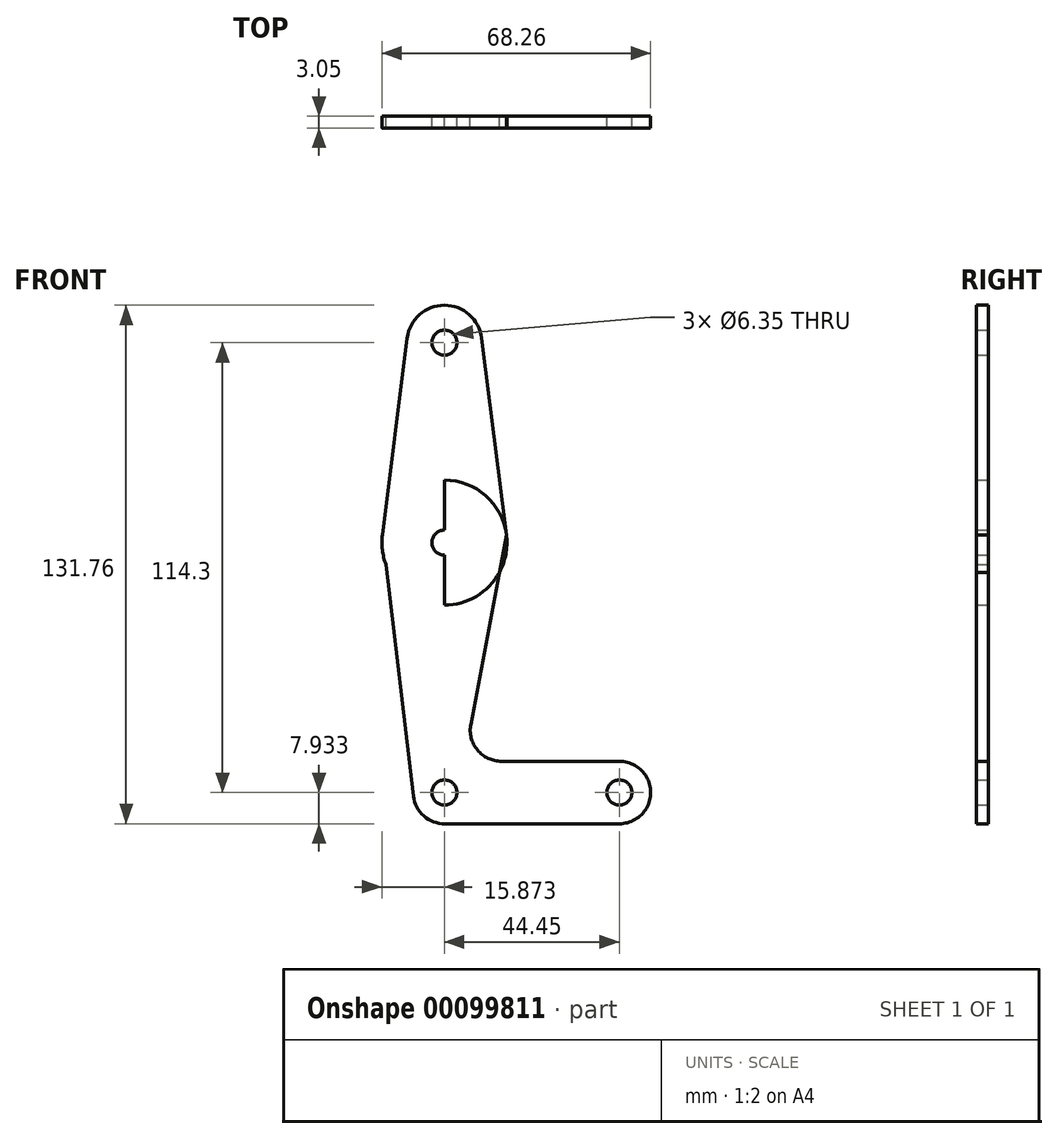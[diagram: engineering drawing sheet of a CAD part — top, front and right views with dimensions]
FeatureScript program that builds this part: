
annotation { "Feature Type Name" : "Feature", "Feature Type Description" : "" }
export const myFeature = defineFeature(function(context is Context, id is Id, definition is map)
    precondition{}
    {
        {
            var Q0;
            Q0=qCreatedBy(makeId("Front.planeOp"),FACE);
            var sketch = newSketch(context, id + "F0", { "sketchPlane" : qUnion([Q0])});
            skLineSegment(sketch, "E0", {"start": v(7.52, 95.91) * mm, "end": v(7.52, -18.39) * mm});
            skLineSegment(sketch, "E1", {"start": v(7.52, -18.39) * mm, "end": v(51.97, -18.39) * mm});
            skCircle(sketch, "E2", {"center": v(7.52, 95.91) * mm, "radius": 9.53 * mm});
            skCircle(sketch, "E3", {"center": v(7.52, 45.11) * mm, "radius": 15.88 * mm});
            skCircle(sketch, "E4", {"center": v(7.52, -18.39) * mm, "radius": 7.94 * mm});
            skCircle(sketch, "E5", {"center": v(51.97, -18.39) * mm, "radius": 7.94 * mm});
            skLineSegment(sketch, "E6", {"start": v(-1.93, 97.1) * mm, "end": v(-8.23, 47.1) * mm});
            skLineSegment(sketch, "E7", {"start": v(-8.23, 47.1) * mm, "end": v(-0.36, -19.32) * mm});
            skLineSegment(sketch, "E8", {"start": v(14.22, -1.03) * mm, "end": v(23.27, 47.1) * mm});
            skLineSegment(sketch, "E9", {"start": v(23.27, 47.1) * mm, "end": v(16.97, 97.1) * mm});
            skLineSegment(sketch, "E10", {"start": v(22.03, -10.45) * mm, "end": v(51.97, -10.45) * mm});
            skLineSegment(sketch, "E11", {"start": v(7.6, -26.32) * mm, "end": v(51.97, -26.32) * mm});
            skCircle(sketch, "E12", {"center": v(7.52, 95.91) * mm, "radius": 3.18 * mm});
            skCircle(sketch, "E13", {"center": v(7.52, 45.11) * mm, "radius": 3.18 * mm});
            skCircle(sketch, "E14", {"center": v(7.52, -18.39) * mm, "radius": 3.18 * mm});
            skCircle(sketch, "E15", {"center": v(51.97, -18.39) * mm, "radius": 3.18 * mm});
            skArc(sketch, "E16.filletArc", {"start": v(14.22, -1.03) * mm, "mid": v(15.91, -7.57) * mm, "end": v(22.03, -10.45) * mm});
            skSolve(sketch);
        }
        {
            var Q0;
            {var subQ3=sQuery(id+"F0.wireOp",EDGE,"E4");var subQ7=sQuery(id+"F0.wireOp",EDGE,"E0");var subQ8=makeQuery(id+"F0.imprint","INTERSECT",VERTEX,{"derivedFrom":[subQ7,subQ3]});Q0=makeQuery(id+"F0.imprint","IMPRINT",FACE,{"disambiguationData":[TD([[makeQuery(id+"F0.imprint","IMPRINT",EDGE,{"disambiguationData":[TD([[subQ8,-1.0]])],"derivedFrom":subQ7}),-1.0]])]});}
            var Q1;
            {var subQ10=sQuery(id+"F0.wireOp",EDGE,"E10");Q1=makeQuery(id+"F0.imprint","IMPRINT",FACE,{"disambiguationData":[TD([[makeQuery(id+"F0.imprint","IMPRINT",EDGE,{"derivedFrom":subQ10}),-1.0]])]});}
            var Q2;
            Q2=makeQuery(id+"F0.imprint","IMPRINT",FACE,{"disambiguationData":[TD([[makeQuery(id+"F0.imprint","IMPRINT",EDGE,{"derivedFrom":sQuery(id+"F0.wireOp",EDGE,"E12")}),-1.0]])]});
            var Q3;
            Q3=makeQuery(id+"F0.imprint","IMPRINT",FACE,{"disambiguationData":[TD([[makeQuery(id+"F0.imprint","IMPRINT",EDGE,{"derivedFrom":sQuery(id+"F0.wireOp",EDGE,"E15")}),-1.0]])]});
            var Q4;
            {var subQ1=sQuery(id+"F0.wireOp",EDGE,"E3");var subQ3=sQuery(id+"F0.wireOp",EDGE,"E0");var subQ4=makeQuery(id+"F0.imprint","INTERSECT",VERTEX,{"disambiguationData":[OD(0.0)],"derivedFrom":[subQ3,subQ1]});Q4=makeQuery(id+"F0.imprint","IMPRINT",FACE,{"disambiguationData":[TD([[makeQuery(id+"F0.imprint","IMPRINT",EDGE,{"disambiguationData":[TD([[subQ4,-1.0]])],"derivedFrom":subQ3}),1.0]])]});}
            var Q5;
            {var subQ0=sQuery(id+"F0.wireOp",EDGE,"E8");var subQ1=sQuery(id+"F0.wireOp",EDGE,"E3");var subQ3=makeQuery(id+"F0.imprint","INTERSECT",VERTEX,{"derivedFrom":[subQ1,subQ0]});Q5=makeQuery(id+"F0.imprint","IMPRINT",FACE,{"disambiguationData":[TD([[makeQuery(id+"F0.imprint","IMPRINT",EDGE,{"disambiguationData":[TD([[subQ3,-1.0]])],"derivedFrom":subQ1}),1.0]])]});}
            var Q6;
            {var subQ5=sQuery(id+"F0.wireOp",EDGE,"E9");Q6=makeQuery(id+"F0.imprint","IMPRINT",FACE,{"disambiguationData":[TD([[makeQuery(id+"F0.imprint","IMPRINT",EDGE,{"derivedFrom":subQ5}),1.0]])]});}
            var Q7;
            {var subQ0=sQuery(id+"F0.wireOp",EDGE,"E4");var subQ1=sQuery(id+"F0.wireOp",EDGE,"E0");var subQ2=makeQuery(id+"F0.imprint","INTERSECT",VERTEX,{"derivedFrom":[subQ1,subQ0]});Q7=makeQuery(id+"F0.imprint","IMPRINT",FACE,{"disambiguationData":[TD([[makeQuery(id+"F0.imprint","IMPRINT",EDGE,{"disambiguationData":[TD([[subQ2,-1.0]])],"derivedFrom":subQ1}),1.0]])]});}
            var Q8;
            {var subQ5=sQuery(id+"F0.wireOp",EDGE,"E11");Q8=makeQuery(id+"F0.imprint","IMPRINT",FACE,{"disambiguationData":[TD([[makeQuery(id+"F0.imprint","IMPRINT",EDGE,{"derivedFrom":subQ5}),1.0]])]});}
            var Q9;
            {var subQ1=sQuery(id+"F0.wireOp",EDGE,"E3");var subQ3=sQuery(id+"F0.wireOp",EDGE,"E0");var subQ4=makeQuery(id+"F0.imprint","INTERSECT",VERTEX,{"disambiguationData":[OD(0.0)],"derivedFrom":[subQ3,subQ1]});Q9=makeQuery(id+"F0.imprint","IMPRINT",FACE,{"disambiguationData":[TD([[makeQuery(id+"F0.imprint","IMPRINT",EDGE,{"disambiguationData":[TD([[subQ4,-1.0]])],"derivedFrom":subQ3}),-1.0]])]});}
            var Q10;
            {var subQ5=sQuery(id+"F0.wireOp",EDGE,"E6");Q10=makeQuery(id+"F0.imprint","IMPRINT",FACE,{"disambiguationData":[TD([[makeQuery(id+"F0.imprint","IMPRINT",EDGE,{"derivedFrom":subQ5}),1.0]])]});}
            var Q11;
            {var subQ0=sQuery(id+"F0.wireOp",EDGE,"E3");var subQ1=sQuery(id+"F0.wireOp",EDGE,"E0");var subQ2=makeQuery(id+"F0.imprint","INTERSECT",VERTEX,{"disambiguationData":[OD(1.0)],"derivedFrom":[subQ1,subQ0]});Q11=makeQuery(id+"F0.imprint","IMPRINT",FACE,{"disambiguationData":[TD([[makeQuery(id+"F0.imprint","IMPRINT",EDGE,{"disambiguationData":[TD([[subQ2,-1.0]])],"derivedFrom":subQ1}),-1.0]])]});}
            var Q12;
            {var subQ0=sQuery(id+"F0.wireOp",EDGE,"E7");var subQ1=sQuery(id+"F0.wireOp",EDGE,"E3");var subQ3=makeQuery(id+"F0.imprint","INTERSECT",VERTEX,{"derivedFrom":[subQ1,subQ0]});Q12=makeQuery(id+"F0.imprint","IMPRINT",FACE,{"disambiguationData":[TD([[makeQuery(id+"F0.imprint","IMPRINT",EDGE,{"disambiguationData":[TD([[subQ3,1.0]])],"derivedFrom":subQ1}),1.0]])]});}
            extrude(context, id + "F1", {"entities" : qUnion([Q0, Q1, Q2, Q3, Q4, Q5, Q6, Q7, Q8, Q9, Q10, Q11, Q12]), "depth" : 3.05 * mm});
        }
    });
